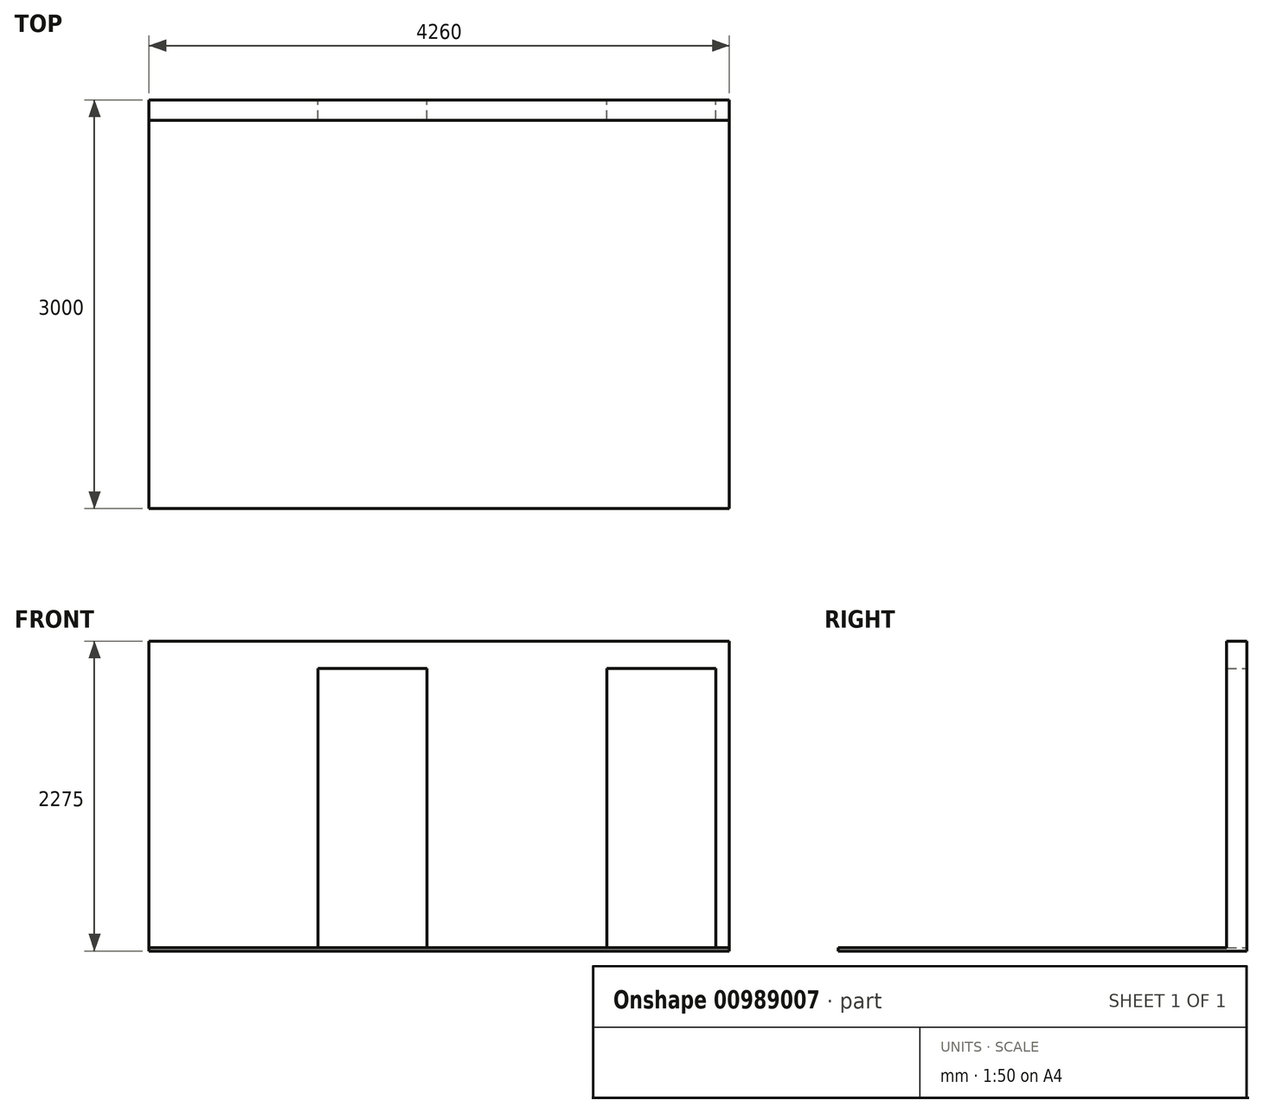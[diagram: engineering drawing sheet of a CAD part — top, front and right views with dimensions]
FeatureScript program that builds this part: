
annotation { "Feature Type Name" : "Feature", "Feature Type Description" : "" }
export const myFeature = defineFeature(function(context is Context, id is Id, definition is map)
    precondition{}
    {
        {
            var Q0;
            Q0=qCreatedBy(makeId("Front.planeOp"),FACE);
            var sketch = newSketch(context, id + "F0", { "sketchPlane" : qUnion([Q0])});
            skLineSegment(sketch, "E0.bottom", {"start": v(-2551.85, 1244.92) * mm, "end": v(1708.15, 1244.92) * mm});
            skLineSegment(sketch, "E0.left", {"start": v(-2551.85, 1244.92) * mm, "end": v(-2551.85, -1005.08) * mm});
            skLineSegment(sketch, "E0.right", {"start": v(1708.15, 1244.92) * mm, "end": v(1708.15, -1005.08) * mm});
            skLineSegment(sketch, "E1", {"start": v(-2551.85, -1005.08) * mm, "end": v(-1311.85, -1005.08) * mm});
            skLineSegment(sketch, "E2", {"start": v(-1311.85, -1005.08) * mm, "end": v(-1311.85, 1044.92) * mm});
            skLineSegment(sketch, "E3", {"start": v(-1311.85, 1044.92) * mm, "end": v(-511.85, 1044.92) * mm});
            skLineSegment(sketch, "E4", {"start": v(-511.85, 1044.92) * mm, "end": v(-511.85, -1005.08) * mm});
            skLineSegment(sketch, "E5", {"start": v(-511.85, -1005.08) * mm, "end": v(808.15, -1005.08) * mm});
            skLineSegment(sketch, "E6", {"start": v(808.15, -1005.08) * mm, "end": v(808.15, 1044.92) * mm});
            skLineSegment(sketch, "E7", {"start": v(808.15, 1044.92) * mm, "end": v(1608.15, 1044.92) * mm});
            skLineSegment(sketch, "E8", {"start": v(1608.15, 1044.92) * mm, "end": v(1608.15, -1005.08) * mm});
            skLineSegment(sketch, "E9", {"start": v(1608.15, -1005.08) * mm, "end": v(1708.15, -1005.08) * mm});
            skSolve(sketch);
        }
        {
            var Q0;
            Q0=qSketchRegion(id+"F0",true);
            extrude(context, id + "F1", {"entities" : qUnion([Q0]), "depth" : 150 * mm, "offsetDistance" : 25 * mm});
        }
        {
            var Q0;
            Q0=makeQuery(id+"F1.opExtrude","SWEPT_FACE",FACE,{"disambiguationData":[OSD([sQuery(id+"F0.wireOp",EDGE,"E1")])]});
            var sketch = newSketch(context, id + "F2", { "sketchPlane" : qUnion([Q0])});
            skLineSegment(sketch, "E10.bottom", {"start": v(-2551.85, 0) * mm, "end": v(1708.15, 0) * mm});
            skLineSegment(sketch, "E10.top", {"start": v(-2551.85, 3000) * mm, "end": v(1708.15, 3000) * mm});
            skLineSegment(sketch, "E10.left", {"start": v(-2551.85, 0) * mm, "end": v(-2551.85, 3000) * mm});
            skLineSegment(sketch, "E10.right", {"start": v(1708.15, 0) * mm, "end": v(1708.15, 3000) * mm});
            skSolve(sketch);
        }
        {
            var Q0;
            Q0=qSketchRegion(id+"F2",true);
            extrude(context, id + "F3", {"entities" : qUnion([Q0]), "operationType" : NewBodyOperationType.ADD, "depth" : 25 * mm, "offsetDistance" : 25 * mm});
        }
    });
